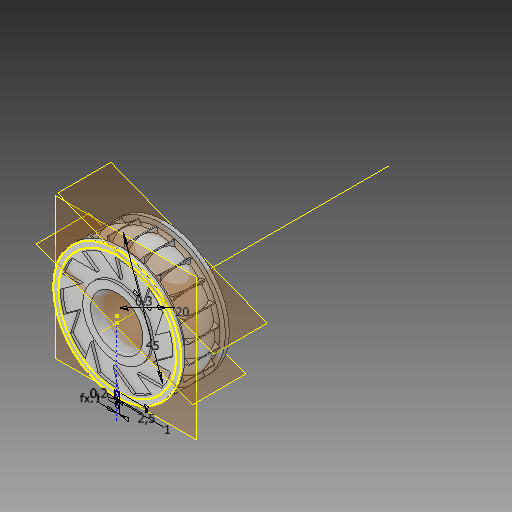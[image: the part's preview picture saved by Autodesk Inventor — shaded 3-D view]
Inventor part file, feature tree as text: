
AUTODESK INVENTOR PART (.ipt)
format: ipt  version: 2017 (Build 210142000, 142)  size: 616,448 bytes
history: native  units: mm
features: reference x80, sketch x10, extrude x9, other x8, plane x4, pattern_circular x2, projected_geometry x2, revolve x1, chamfer x1
ambient origin geometry x8: Origin, YZ Plane, XZ Plane, XY Plane, X Axis, Y Axis, Z Axis, Center Point
bodies: Solid1 (feature_tree)
feature tree (117):
  extrude  "Extrusion1"  Depth=45.0mm
  plane  "Work Plane3"
  revolve  "Revolution1"  [1 undecoded]
  sketch  "Sketch3"  dims[d7=1.5mm d8=1.5mm]
  plane  "Work Plane4"
  extrude  "Extrusion3"  Depth=1.5mm
  other  "Work Axis1"
  pattern_circular  "Circular Pattern1"  [2 undecoded]
  sketch  "Sketch6"  dims[d10=2.0mm]
  extrude  "Extrusion4"  [1 undecoded]
  extrude  "Extrusion5"  Depth=0.2mm
  extrude  "Extrusion6"  Depth=11.5mm TaperAngle=0.0deg
  extrude  "Extrusion7"  Depth=12.5mm TaperAngle=360.0deg
  pattern_circular  "Circular Pattern2"  [2 undecoded]
  extrude  "Extrusion8"  Depth=12.5mm TaperAngle=0.0deg
  extrude  "Extrusion11"  Depth=2.5mm
  extrude  "Extrusion12"  Depth=12.5mm TaperAngle=0.0deg
  chamfer  "Chamfer3"  Distance=3.0mm
  sketch  "Sketch1"  dims[d0=0.3mm d1=45.0mm]
  reference  "Reference1"
  reference  "Reference2"
  reference  "Reference3"
  reference  "Reference4"
  reference  "Reference5"
  reference  "Reference6"
  reference  "Reference7"
  reference  "Reference8"
  reference  "Reference9"
  reference  "Reference10"
  reference  "Reference11"
  reference  "Reference12"
  reference  "Reference13"
  reference  "Reference14"
  reference  "Reference15"
  reference  "Reference16"
  reference  "Reference17"
  reference  "Reference18"
  reference  "Reference19"
  reference  "Reference20"
  reference  "Reference21"
  reference  "Reference22"
  reference  "Reference23"
  reference  "Reference24"
  reference  "Reference25"
  reference  "Reference26"
  reference  "Reference27"
  reference  "Reference28"
  reference  "Reference29"
  reference  "Reference30"
  reference  "Reference31"
  reference  "Reference32"
  reference  "Reference33"
  reference  "Reference34"
  reference  "Reference35"
  reference  "Reference36"
  reference  "Reference37"
  reference  "Reference38"
  reference  "Reference39"
  reference  "Reference40"
  reference  "Reference41"
  reference  "Reference42"
  reference  "Reference43"
  reference  "Reference44"
  reference  "Reference45"
  reference  "Reference46"
  reference  "Reference47"
  reference  "Reference48"
  reference  "Reference49"
  reference  "Reference50"
  reference  "Reference51"
  reference  "Reference52"
  reference  "Reference53"
  reference  "Reference54"
  reference  "Reference55"
  reference  "Reference56"
  reference  "Reference57"
  reference  "Reference58"
  reference  "Reference59"
  reference  "Reference60"
  reference  "Reference61"
  reference  "Reference62"
  reference  "Reference63"
  reference  "Reference64"
  reference  "Reference65"
  reference  "Reference66"
  reference  "Reference67"
  reference  "Reference68"
  reference  "Reference69"
  reference  "Reference70"
  reference  "Reference71"
  reference  "Reference72"
  reference  "Reference73"
  reference  "Reference74"
  reference  "Reference75"
  reference  "Reference76"
  reference  "Reference77"
  reference  "Reference78"
  reference  "Reference79"
  reference  "Reference80"
  plane  "Work Plane1"
  plane  "Work Plane2"
  sketch  "Sketch2"  dims[d2=20.0mm d3=10.0mm d4=8.5mm d5=0.0mm d6=0.0mm]
  projected_geometry  "Projected Loop1"
  sketch  "Sketch5"  dims[d9=2.0mm]
  sketch  "Sketch7"  dims[d11=2.0mm]
  projected_geometry  "Projected Loop2"
  sketch  "Sketch8"  dims[d12=2.0mm]
  sketch  "Sketch9"  dims[d13=90.0deg]
  sketch  "Sketch14"  dims[d14=2.5mm]
  sketch  "Sketch15"  dims[d15=1.0mm d16=1.0mm d17=-3.5mm d20=0.2mm d21=11.5mm d22=0.0mm d23=220.0mm d24=360.0deg d26=12.5mm d27=0.0mm d28=9.5mm d29=0.0mm d30=2.5mm d31=4.0mm d32=0.0mm d34=3.0mm d36=3.0mm d37=90.0deg d38=7.0mm d39=1.0mm d40=0.0mm d41=100.0mm d42=360.0deg d47=13.0mm d48=0.0mm d58=7.0mm d59=0.0mm d60=4.5mm d61=7.0mm d62=0.0mm d63=12.5mm d64=4.0mm d65=45.0deg]
  other  "<userpath>\Desktop\3d\scanning-robot\Assembly1.iam"
  other  "Assembly1.iam"
  other  "Tower Pro MG90S Micro servo:2"
  other  "Цилиндрическое зубчатое зацепление:5"
  other  "Цилиндрическое зубчатое зацепление2:1"
  other  "Assembly1"
  other  "base:1"
note: 6 required parameter values undecoded (feature->parameter linkage not recoverable at this tier; creation-order binding heuristic only, values carry confidence <= 0.55)